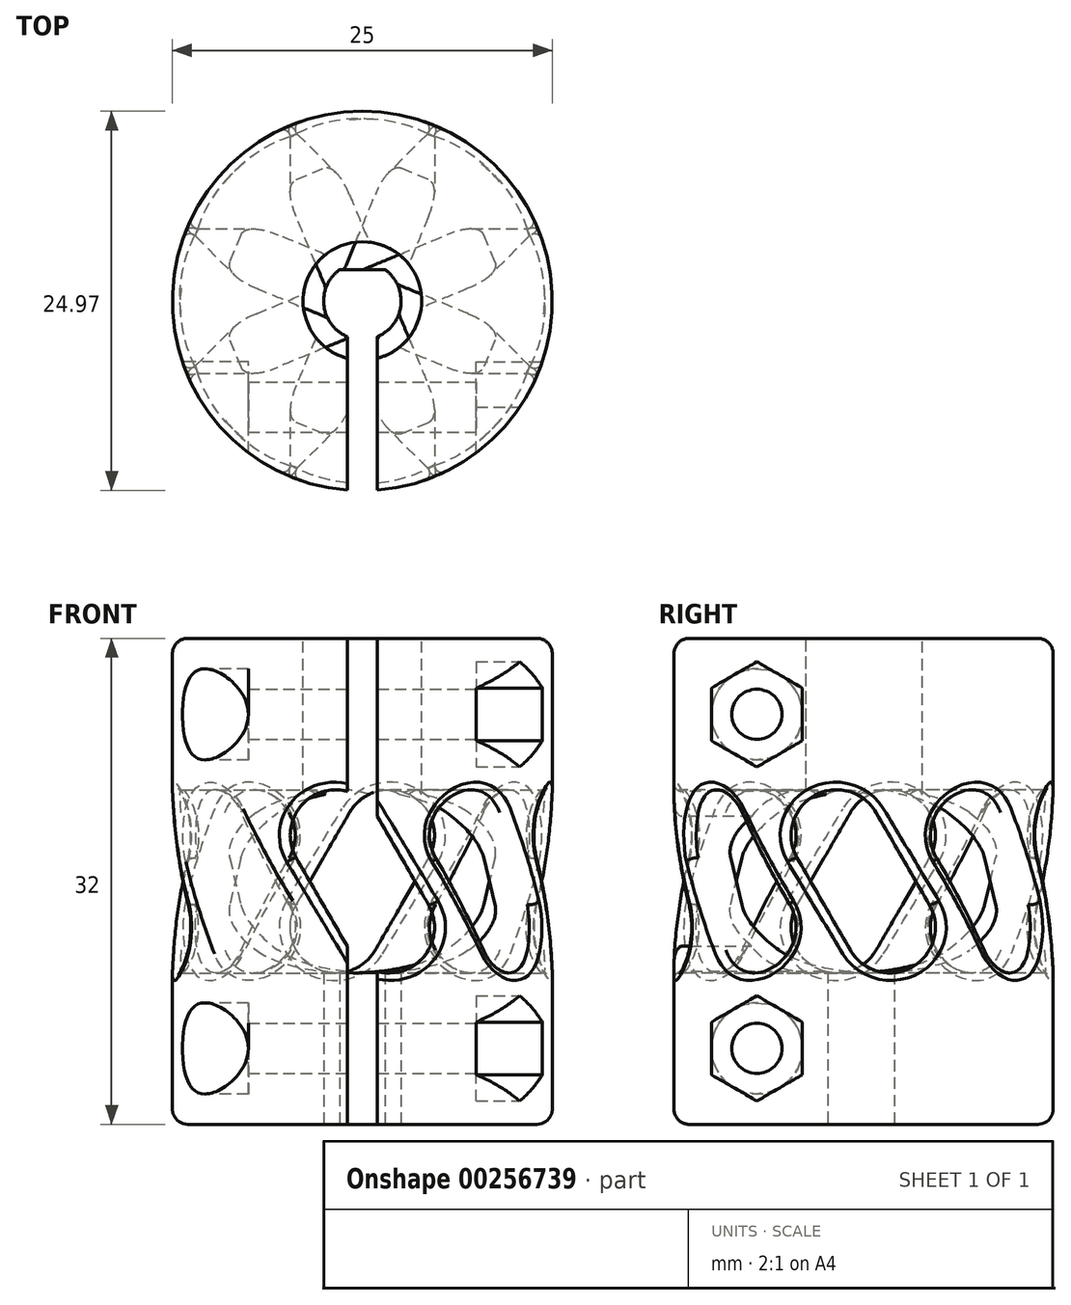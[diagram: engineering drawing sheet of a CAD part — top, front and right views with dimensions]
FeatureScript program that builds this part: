
annotation { "Feature Type Name" : "Feature", "Feature Type Description" : "" }
export const myFeature = defineFeature(function(context is Context, id is Id, definition is map)
    precondition{}
    {
        {
            var Q0;
            Q0=qCreatedBy(makeId("Top.planeOp"),FACE);
            var sketch = newSketch(context, id + "F0", { "sketchPlane" : qUnion([Q0])});
            skCircle(sketch, "E0", {"center": v(0, 0) * mm, "radius": 12.5 * mm});
            skSolve(sketch);
        }
        {
            var Q0;
            Q0 = qSketchRegion(id + "F0", true);
            extrude(context, id + "F1", {"entities" : qUnion([Q0]), "depth" : 32 * mm});
        }
        {
            var Q0;
            Q0=makeQuery(id+"F1.opExtrude","CAP_FACE",FACE,{"disambiguationData":[OSD([sQuery(id+"F0.wireOp",EDGE,"E0")])],"isStart":false});
            var sketch = newSketch(context, id + "F2", { "sketchPlane" : qUnion([Q0])});
            skCircle(sketch, "E1", {"center": v(0, 0) * mm, "radius": 3.9 * mm});
            skSolve(sketch);
        }
        {
            var Q0;
            Q0 = qSketchRegion(id + "F2", true);
            extrude(context, id + "F3", {"entities" : qUnion([Q0]), "operationType" : NewBodyOperationType.REMOVE, "oppositeDirection" : true, "depth" : 20 * mm});
        }
        {
            var Q0;
            Q0=makeQuery(id+"F1.opExtrude","CAP_FACE",FACE,{"disambiguationData":[OSD([sQuery(id+"F0.wireOp",EDGE,"E0")])],"isStart":true});
            var sketch = newSketch(context, id + "F4", { "sketchPlane" : qUnion([Q0])});
            skArc(sketch, "E2", {"start": v(1.5, -2.06) * mm, "mid": v(0, 2.55) * mm, "end": v(-1.5, -2.06) * mm});
            skLineSegment(sketch, "E3", {"start": v(-1.5, -2.06) * mm, "end": v(1.5, -2.06) * mm});
            skLineSegment(sketch, "E4", {"start": v(0, 0) * mm, "end": v(0, -2.06) * mm, "construction": true});
            skSolve(sketch);
        }
        {
            var Q0;
            Q0 = qSketchRegion(id + "F4", true);
            extrude(context, id + "F5", {"entities" : qUnion([Q0]), "operationType" : NewBodyOperationType.REMOVE, "endBound" : BoundingType.THROUGH_ALL, "oppositeDirection" : true, "depth" : 25 * mm});
        }
        {
            var Q0;
            Q0=qCreatedBy(makeId("Front.planeOp"),FACE);
            cPlane(context, id + "F6", {"entities" : qUnion([Q0]), "cplaneType" : CPlaneType.OFFSET, "offset" : 12.5 * mm, "width" : 150 * mm, "height" : 150 * mm});
        }
        {
            var Q0;
            Q0=qCreatedBy(id+"F6.planeOp",FACE);
            var sketch = newSketch(context, id + "F7", { "sketchPlane" : qUnion([Q0])});
            skLineSegment(sketch, "E5", {"start": v(0, 0) * mm, "end": v(0, 16) * mm, "construction": true});
            skLineSegment(sketch, "E6", {"start": v(-1.75, 19.03) * mm, "end": v(1.75, 12.97) * mm, "construction": true});
            skArc(sketch, "E7", {"start": v(0.85, 20.53) * mm, "mid": v(-3.25, 21.63) * mm, "end": v(-4.35, 17.53) * mm});
            skArc(sketch, "E8", {"start": v(-0.85, 11.47) * mm, "mid": v(3.25, 10.37) * mm, "end": v(4.35, 14.47) * mm});
            skLineSegment(sketch, "E9", {"start": v(0.85, 20.53) * mm, "end": v(4.35, 14.47) * mm});
            skLineSegment(sketch, "E10", {"start": v(-4.35, 17.53) * mm, "end": v(-0.85, 11.47) * mm});
            skSolve(sketch);
        }
        {
            var Q0;
            Q0 = qSketchRegion(id + "F7", true);
            extrude(context, id + "F8", {"entities" : qUnion([Q0]), "operationType" : NewBodyOperationType.REMOVE, "oppositeDirection" : true, "depth" : 12.5 * mm});
        }
        {
            var Q0;
            Q0=makeQuery(id+"F1.opExtrude","CAP_EDGE",EDGE,{"disambiguationData":[OSD([sQuery(id+"F0.wireOp",EDGE,"E0")])],"isStart":true});
            var Q1;
            Q1=makeQuery(id+"F1.opExtrude","CAP_EDGE",EDGE,{"disambiguationData":[OSD([sQuery(id+"F0.wireOp",EDGE,"E0")])],"isStart":false});
            fillet(context, id + "F9", {"entities" : qUnion([Q0, Q1]), "radius" : 1 * mm, "tangentPropagation" : true, "allowEdgeOverflow" : false});
        }
        {
            var Q0;
            Q0=makeQuery(id+"F1.opExtrude","CAP_FACE",FACE,{"disambiguationData":[OSD([sQuery(id+"F0.wireOp",EDGE,"E0")])],"isStart":false});
            var sketch = newSketch(context, id + "F10", { "sketchPlane" : qUnion([Q0])});
            skLineSegment(sketch, "E11", {"start": v(0, 0) * mm, "end": v(0, -15) * mm, "construction": true});
            skLineSegment(sketch, "E12", {"start": v(0, -15) * mm, "end": v(1, -15) * mm});
            skLineSegment(sketch, "E13", {"start": v(1, -15) * mm, "end": v(1, 0) * mm});
            skLineSegment(sketch, "E14", {"start": v(1, 0) * mm, "end": v(0, 0) * mm});
            skLineSegment(sketch, "E15", {"start": v(-1, 0) * mm, "end": v(-1, -15) * mm});
            skLineSegment(sketch, "E16", {"start": v(-1, -15) * mm, "end": v(0, -15) * mm});
            skLineSegment(sketch, "E17", {"start": v(-1, 0) * mm, "end": v(0, 0) * mm});
            skSolve(sketch);
        }
        {
            var Q0;
            Q0 = qSketchRegion(id + "F10", true);
            extrude(context, id + "F11", {"entities" : qUnion([Q0]), "operationType" : NewBodyOperationType.REMOVE, "endBound" : BoundingType.THROUGH_ALL, "oppositeDirection" : true, "depth" : 25 * mm});
        }
        {
            var Q0;
            Q0=qCreatedBy(makeId("Right.planeOp"),FACE);
            cPlane(context, id + "F12", {"entities" : qUnion([Q0]), "cplaneType" : CPlaneType.OFFSET, "offset" : 12.5 * mm, "width" : 150 * mm, "height" : 150 * mm});
        }
        {
            var Q0;
            Q0=qCreatedBy(id+"F12.planeOp",FACE);
            var sketch = newSketch(context, id + "F13", { "sketchPlane" : qUnion([Q0])});
            skLineSegment(sketch, "E18", {"start": v(0, 0) * mm, "end": v(0, 16) * mm, "construction": true});
            skLineSegment(sketch, "E19", {"start": v(0, 0) * mm, "end": v(-7, 0) * mm, "construction": true});
            skLineSegment(sketch, "E20", {"start": v(-7, 0) * mm, "end": v(-7, 32) * mm, "construction": true});
            skCircle(sketch, "E21", {"center": v(-7, 5) * mm, "radius": 1.65 * mm});
            skCircle(sketch, "E22", {"center": v(-7, 27) * mm, "radius": 1.65 * mm});
            skLineSegment(sketch, "E23", {"start": v(-1.75, 19.03) * mm, "end": v(1.75, 12.97) * mm, "construction": true});
            skArc(sketch, "E24", {"start": v(0.85, 20.53) * mm, "mid": v(-3.25, 21.63) * mm, "end": v(-4.35, 17.53) * mm});
            skArc(sketch, "E25", {"start": v(-0.85, 11.47) * mm, "mid": v(3.25, 10.37) * mm, "end": v(4.35, 14.47) * mm});
            skLineSegment(sketch, "E26.0", {"start": v(0.85, 20.53) * mm, "end": v(4.35, 14.47) * mm});
            skLineSegment(sketch, "E27.0", {"start": v(-4.35, 17.53) * mm, "end": v(-0.85, 11.47) * mm});
            skSolve(sketch);
        }
        {
            var Q0;
            Q0 = qSketchRegion(id + "F13", true);
            extrude(context, id + "F14", {"entities" : qUnion([Q0]), "operationType" : NewBodyOperationType.REMOVE, "oppositeDirection" : true, "depth" : 12.5 * mm});
        }
        {
            var Q0;
            Q0=qCreatedBy(id+"F12.planeOp",FACE);
            var sketch = newSketch(context, id + "F15", { "sketchPlane" : qUnion([Q0])});
            skLineSegment(sketch, "E28", {"start": v(0, 0) * mm, "end": v(-7, 0) * mm, "construction": true});
            skLineSegment(sketch, "E29", {"start": v(-7, 0) * mm, "end": v(-7, 32) * mm, "construction": true});
            skCircle(sketch, "E30.cCircle", {"center": v(-7, 5) * mm, "radius": 3 * mm, "construction": true});
            skLineSegment(sketch, "E30.0", {"start": v(-4, 6.73) * mm, "end": v(-4, 3.27) * mm});
            skLineSegment(sketch, "E30.1", {"start": v(-4, 3.27) * mm, "end": v(-7, 1.54) * mm});
            skLineSegment(sketch, "E30.2", {"start": v(-7, 1.54) * mm, "end": v(-10, 3.27) * mm});
            skLineSegment(sketch, "E30.3", {"start": v(-10, 3.27) * mm, "end": v(-10, 6.73) * mm});
            skLineSegment(sketch, "E30.4", {"start": v(-10, 6.73) * mm, "end": v(-7, 8.46) * mm});
            skLineSegment(sketch, "E30.5", {"start": v(-7, 8.46) * mm, "end": v(-4, 6.73) * mm});
            skPoint(sketch, "E30.0.midPoint", {"position": v(-4, 5) * mm});
            skCircle(sketch, "E31.cCircle", {"center": v(-7, 27) * mm, "radius": 3 * mm, "construction": true});
            skLineSegment(sketch, "E31.0", {"start": v(-4, 25.27) * mm, "end": v(-7, 23.54) * mm});
            skLineSegment(sketch, "E31.1", {"start": v(-7, 23.54) * mm, "end": v(-10, 25.27) * mm});
            skLineSegment(sketch, "E31.2", {"start": v(-10, 25.27) * mm, "end": v(-10, 28.73) * mm});
            skLineSegment(sketch, "E31.3", {"start": v(-10, 28.73) * mm, "end": v(-7, 30.46) * mm});
            skLineSegment(sketch, "E31.4", {"start": v(-7, 30.46) * mm, "end": v(-4, 28.73) * mm});
            skLineSegment(sketch, "E31.5", {"start": v(-4, 28.73) * mm, "end": v(-4, 25.27) * mm});
            skPoint(sketch, "E31.0.midPoint", {"position": v(-5.5, 24.4) * mm});
            skSolve(sketch);
        }
        {
            var Q0;
            Q0 = qSketchRegion(id + "F15", true);
            extrude(context, id + "F16", {"entities" : qUnion([Q0]), "operationType" : NewBodyOperationType.REMOVE, "oppositeDirection" : true, "depth" : 5 * mm});
        }
        {
            var Q0;
            Q0=qCreatedBy(makeId("Right.planeOp"),FACE);
            cPlane(context, id + "F17", {"entities" : qUnion([Q0]), "cplaneType" : CPlaneType.OFFSET, "offset" : 12.5 * mm, "oppositeDirection" : true, "width" : 150 * mm, "height" : 150 * mm});
        }
        {
            var Q0;
            Q0=qCreatedBy(id+"F17.planeOp",FACE);
            var sketch = newSketch(context, id + "F18", { "sketchPlane" : qUnion([Q0])});
            skLineSegment(sketch, "E32", {"start": v(0, 0) * mm, "end": v(-7, 0) * mm, "construction": true});
            skLineSegment(sketch, "E33", {"start": v(-7, 0) * mm, "end": v(-7, 32) * mm, "construction": true});
            skCircle(sketch, "E34", {"center": v(-7, 5) * mm, "radius": 3 * mm});
            skCircle(sketch, "E35", {"center": v(-7, 27) * mm, "radius": 3 * mm});
            skSolve(sketch);
        }
        {
            var Q0;
            Q0 = qSketchRegion(id + "F18", true);
            extrude(context, id + "F19", {"entities" : qUnion([Q0]), "operationType" : NewBodyOperationType.REMOVE, "depth" : 5 * mm});
        }
        {
            var Q0;
            Q0=qCreatedBy(makeId("Front.planeOp"),FACE);
            var sketch = newSketch(context, id + "F20", { "sketchPlane" : qUnion([Q0])});
            skLineSegment(sketch, "E36", {"start": v(0, 0) * mm, "end": v(0, 50) * mm, "construction": true});
            skSolve(sketch);
        }
        {
            var Q0;
            Q0=sQuery(id+"F20.wireOp",EDGE,"E36");
            cPlane(context, id + "F21", {"entities" : qUnion([Q0]), "cplaneType" : CPlaneType.LINE_ANGLE, "offset" : 25 * mm, "angle" : 45 * degree, "width" : 150 * mm, "height" : 150 * mm});
        }
        {
            var Q0;
            Q0=qCreatedBy(id+"F21.planeOp",FACE);
            var sketch = newSketch(context, id + "F22", { "sketchPlane" : qUnion([Q0])});
            skLineSegment(sketch, "E37", {"start": v(0, 0) * mm, "end": v(0, 16) * mm, "construction": true});
            skLineSegment(sketch, "E38", {"start": v(1.75, 19.03) * mm, "end": v(-1.75, 12.97) * mm, "construction": true});
            skArc(sketch, "E39", {"start": v(4.35, 17.53) * mm, "mid": v(3.25, 21.63) * mm, "end": v(-0.85, 20.53) * mm});
            skArc(sketch, "E40", {"start": v(-4.35, 14.47) * mm, "mid": v(-3.25, 10.37) * mm, "end": v(0.85, 11.47) * mm});
            skLineSegment(sketch, "E41.0", {"start": v(4.35, 17.53) * mm, "end": v(0.85, 11.47) * mm});
            skLineSegment(sketch, "E42.0", {"start": v(-0.85, 20.53) * mm, "end": v(-4.35, 14.47) * mm});
            skSolve(sketch);
        }
        {
            var Q0;
            Q0 = qSketchRegion(id + "F22", true);
            extrude(context, id + "F23", {"entities" : qUnion([Q0]), "operationType" : NewBodyOperationType.REMOVE, "endBound" : BoundingType.THROUGH_ALL, "oppositeDirection" : true, "depth" : 25 * mm});
        }
        {
            var Q0;
            Q0=sQuery(id+"F20.wireOp",EDGE,"E36");
            cPlane(context, id + "F24", {"entities" : qUnion([Q0]), "cplaneType" : CPlaneType.LINE_ANGLE, "offset" : 25 * mm, "angle" : 135 * degree, "width" : 150 * mm, "height" : 150 * mm});
        }
        {
            var Q0;
            Q0=qCreatedBy(id+"F24.planeOp",FACE);
            var sketch = newSketch(context, id + "F25", { "sketchPlane" : qUnion([Q0])});
            skLineSegment(sketch, "E43", {"start": v(0, 0) * mm, "end": v(0, 16) * mm, "construction": true});
            skLineSegment(sketch, "E44", {"start": v(1.75, 12.97) * mm, "end": v(-1.75, 19.03) * mm, "construction": true});
            skArc(sketch, "E45", {"start": v(-0.85, 11.47) * mm, "mid": v(3.25, 10.37) * mm, "end": v(4.35, 14.47) * mm});
            skArc(sketch, "E46", {"start": v(0.85, 20.53) * mm, "mid": v(-3.25, 21.63) * mm, "end": v(-4.35, 17.53) * mm});
            skLineSegment(sketch, "E47.0", {"start": v(4.35, 14.47) * mm, "end": v(0.85, 20.53) * mm});
            skLineSegment(sketch, "E48.0", {"start": v(-0.85, 11.47) * mm, "end": v(-4.35, 17.53) * mm});
            skSolve(sketch);
        }
        {
            var Q0;
            Q0 = qSketchRegion(id + "F25", true);
            extrude(context, id + "F26", {"entities" : qUnion([Q0]), "operationType" : NewBodyOperationType.REMOVE, "endBound" : BoundingType.THROUGH_ALL, "depth" : 25 * mm});
        }
        {
            var Q0;
            Q0=qCreatedBy(id+"F24.planeOp",FACE);
            var sketch = newSketch(context, id + "F27", { "sketchPlane" : qUnion([Q0])});
            skLineSegment(sketch, "E49", {"start": v(0, 0) * mm, "end": v(0, 16) * mm, "construction": true});
            skLineSegment(sketch, "E50", {"start": v(1.75, 19.03) * mm, "end": v(-1.75, 12.97) * mm, "construction": true});
            skArc(sketch, "E51", {"start": v(4.35, 17.53) * mm, "mid": v(3.25, 21.63) * mm, "end": v(-0.85, 20.53) * mm});
            skArc(sketch, "E52", {"start": v(-4.35, 14.47) * mm, "mid": v(-3.25, 10.37) * mm, "end": v(0.85, 11.47) * mm});
            skLineSegment(sketch, "E53.0", {"start": v(-0.85, 20.53) * mm, "end": v(-4.35, 14.47) * mm});
            skLineSegment(sketch, "E54.0", {"start": v(4.35, 17.53) * mm, "end": v(0.85, 11.47) * mm});
            skSolve(sketch);
        }
        {
            var Q0;
            Q0 = qSketchRegion(id + "F27", true);
            extrude(context, id + "F28", {"entities" : qUnion([Q0]), "operationType" : NewBodyOperationType.REMOVE, "oppositeDirection" : true, "depth" : 25 * mm});
        }
        {
            var Q0;
            Q0=qCreatedBy(makeId("Right.planeOp"),FACE);
            var sketch = newSketch(context, id + "F29", { "sketchPlane" : qUnion([Q0])});
            skLineSegment(sketch, "E55", {"start": v(0, 0) * mm, "end": v(0, 16) * mm, "construction": true});
            skLineSegment(sketch, "E56", {"start": v(1.75, 19.03) * mm, "end": v(-1.75, 12.97) * mm, "construction": true});
            skArc(sketch, "E57", {"start": v(4.35, 17.53) * mm, "mid": v(3.25, 21.63) * mm, "end": v(-0.85, 20.53) * mm});
            skArc(sketch, "E58", {"start": v(-4.35, 14.47) * mm, "mid": v(-3.25, 10.37) * mm, "end": v(0.85, 11.47) * mm});
            skLineSegment(sketch, "E59.0", {"start": v(4.35, 17.53) * mm, "end": v(0.85, 11.47) * mm});
            skLineSegment(sketch, "E60.0", {"start": v(-0.85, 20.53) * mm, "end": v(-4.35, 14.47) * mm});
            skLineSegment(sketch, "E61", {"start": v(0, 0) * mm, "end": v(-7, 0) * mm, "construction": true});
            skLineSegment(sketch, "E62", {"start": v(-7, 0) * mm, "end": v(-7, 27) * mm, "construction": true});
            skCircle(sketch, "E63", {"center": v(-7, 27) * mm, "radius": 1.65 * mm});
            skCircle(sketch, "E64", {"center": v(-7, 5) * mm, "radius": 1.65 * mm});
            skSolve(sketch);
        }
        {
            var Q0;
            Q0 = qSketchRegion(id + "F29", true);
            extrude(context, id + "F30", {"entities" : qUnion([Q0]), "operationType" : NewBodyOperationType.REMOVE, "oppositeDirection" : true, "depth" : 25 * mm});
        }
        {
            var Q0;
            Q0=qCreatedBy(makeId("Front.planeOp"),FACE);
            var sketch = newSketch(context, id + "F31", { "sketchPlane" : qUnion([Q0])});
            skLineSegment(sketch, "E65", {"start": v(0, 0) * mm, "end": v(0, 16) * mm, "construction": true});
            skLineSegment(sketch, "E66", {"start": v(1.75, 19.03) * mm, "end": v(-1.75, 12.97) * mm, "construction": true});
            skArc(sketch, "E67", {"start": v(4.35, 17.53) * mm, "mid": v(3.25, 21.63) * mm, "end": v(-0.85, 20.53) * mm});
            skArc(sketch, "E68", {"start": v(-4.35, 14.47) * mm, "mid": v(-3.25, 10.37) * mm, "end": v(0.85, 11.47) * mm});
            skLineSegment(sketch, "E69.0", {"start": v(4.35, 17.53) * mm, "end": v(0.85, 11.47) * mm});
            skLineSegment(sketch, "E70.0", {"start": v(-0.85, 20.53) * mm, "end": v(-4.35, 14.47) * mm});
            skSolve(sketch);
        }
        {
            var Q0;
            Q0 = qSketchRegion(id + "F31", true);
            extrude(context, id + "F32", {"entities" : qUnion([Q0]), "operationType" : NewBodyOperationType.REMOVE, "oppositeDirection" : true, "depth" : 25 * mm});
        }
        {
            var Q0;
            Q0=qCreatedBy(id+"F21.planeOp",FACE);
            var sketch = newSketch(context, id + "F33", { "sketchPlane" : qUnion([Q0])});
            skLineSegment(sketch, "E71", {"start": v(0, 0) * mm, "end": v(0, 16) * mm, "construction": true});
            skLineSegment(sketch, "E72", {"start": v(-1.75, 19.03) * mm, "end": v(1.75, 12.97) * mm, "construction": true});
            skArc(sketch, "E73", {"start": v(0.85, 20.53) * mm, "mid": v(-3.25, 21.63) * mm, "end": v(-4.35, 17.53) * mm});
            skArc(sketch, "E74", {"start": v(-0.85, 11.47) * mm, "mid": v(3.25, 10.37) * mm, "end": v(4.35, 14.47) * mm});
            skLineSegment(sketch, "E75.0", {"start": v(-4.35, 17.53) * mm, "end": v(-0.85, 11.47) * mm});
            skLineSegment(sketch, "E76.0", {"start": v(0.85, 20.53) * mm, "end": v(4.35, 14.47) * mm});
            skSolve(sketch);
        }
        {
            var Q0;
            Q0 = qSketchRegion(id + "F33", true);
            extrude(context, id + "F34", {"entities" : qUnion([Q0]), "operationType" : NewBodyOperationType.REMOVE, "depth" : 25 * mm});
        }
        {
            var Q0;
            Q0=makeQuery(id+"F28.boolean.opBoolean","INTERSECT",EDGE,{"derivedFrom":[makeQuery(id+"F1.opExtrude","SWEPT_FACE",FACE,{"disambiguationData":[OSD([sQuery(id+"F0.wireOp",EDGE,"E0")])]}),makeQuery(id+"F28.opExtrude","SWEPT_FACE",FACE,{"disambiguationData":[OSD([sQuery(id+"F27.wireOp",EDGE,"E53.0")])]})]});
            var Q1;
            Q1=makeQuery(id+"F14.boolean.opBoolean","INTERSECT",EDGE,{"derivedFrom":[makeQuery(id+"F1.opExtrude","SWEPT_FACE",FACE,{"disambiguationData":[OSD([sQuery(id+"F0.wireOp",EDGE,"E0")])]}),makeQuery(id+"F14.opExtrude","SWEPT_FACE",FACE,{"disambiguationData":[OSD([sQuery(id+"F13.wireOp",EDGE,"E27.0")])]})]});
            var Q2;
            Q2=makeQuery(id+"F8.boolean.opBoolean","INTERSECT",EDGE,{"derivedFrom":[makeQuery(id+"F1.opExtrude","SWEPT_FACE",FACE,{"disambiguationData":[OSD([sQuery(id+"F0.wireOp",EDGE,"E0")])]}),makeQuery(id+"F8.opExtrude","SWEPT_FACE",FACE,{"disambiguationData":[OSD([sQuery(id+"F7.wireOp",EDGE,"E8")])]})]});
            var Q3;
            Q3=makeQuery(id+"F8.boolean.opBoolean","INTERSECT",EDGE,{"derivedFrom":[makeQuery(id+"F1.opExtrude","SWEPT_FACE",FACE,{"disambiguationData":[OSD([sQuery(id+"F0.wireOp",EDGE,"E0")])]}),makeQuery(id+"F8.opExtrude","SWEPT_FACE",FACE,{"disambiguationData":[OSD([sQuery(id+"F7.wireOp",EDGE,"E10")])]})]});
            var Q4;
            Q4=makeQuery(id+"F23.boolean.opBoolean","INTERSECT",EDGE,{"derivedFrom":[makeQuery(id+"F1.opExtrude","SWEPT_FACE",FACE,{"disambiguationData":[OSD([sQuery(id+"F0.wireOp",EDGE,"E0")])]}),makeQuery(id+"F23.opExtrude","SWEPT_FACE",FACE,{"disambiguationData":[OSD([sQuery(id+"F22.wireOp",EDGE,"E42.0")])]})]});
            var Q5;
            Q5=makeQuery(id+"F30.boolean.opBoolean","INTERSECT",EDGE,{"derivedFrom":[makeQuery(id+"F1.opExtrude","SWEPT_FACE",FACE,{"disambiguationData":[OSD([sQuery(id+"F0.wireOp",EDGE,"E0")])]}),makeQuery(id+"F30.opExtrude","SWEPT_FACE",FACE,{"disambiguationData":[OSD([sQuery(id+"F29.wireOp",EDGE,"E58")])]})]});
            var Q6;
            Q6=makeQuery(id+"F26.boolean.opBoolean","INTERSECT",EDGE,{"derivedFrom":[makeQuery(id+"F1.opExtrude","SWEPT_FACE",FACE,{"disambiguationData":[OSD([sQuery(id+"F0.wireOp",EDGE,"E0")])]}),makeQuery(id+"F26.opExtrude","SWEPT_FACE",FACE,{"disambiguationData":[OSD([sQuery(id+"F25.wireOp",EDGE,"E45")])]})]});
            var Q7;
            Q7=makeQuery(id+"F32.boolean.opBoolean","INTERSECT",EDGE,{"derivedFrom":[makeQuery(id+"F1.opExtrude","SWEPT_FACE",FACE,{"disambiguationData":[OSD([sQuery(id+"F0.wireOp",EDGE,"E0")])]}),makeQuery(id+"F32.opExtrude","SWEPT_FACE",FACE,{"disambiguationData":[OSD([sQuery(id+"F31.wireOp",EDGE,"E68")])]})]});
            var Q8;
            Q8=makeQuery(id+"F34.boolean.opBoolean","INTERSECT",EDGE,{"derivedFrom":[makeQuery(id+"F1.opExtrude","SWEPT_FACE",FACE,{"disambiguationData":[OSD([sQuery(id+"F0.wireOp",EDGE,"E0")])]}),makeQuery(id+"F34.opExtrude","SWEPT_FACE",FACE,{"disambiguationData":[OSD([sQuery(id+"F33.wireOp",EDGE,"E74")])]})]});
            fillet(context, id + "F35", {"entities" : qUnion([Q0, Q1, Q2, Q3, Q4, Q5, Q6, Q7, Q8]), "radius" : 0.5 * mm, "tangentPropagation" : true, "allowEdgeOverflow" : false});
        }
    });
